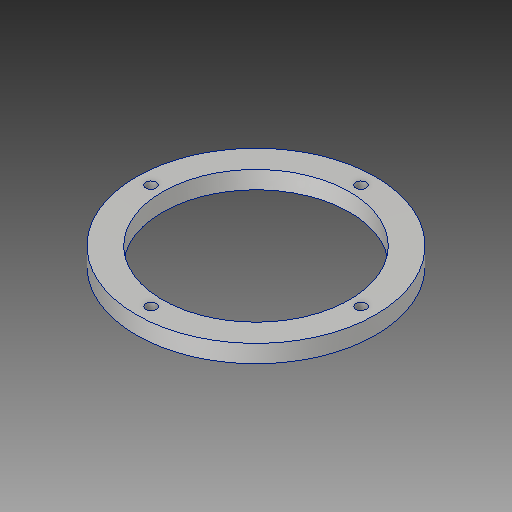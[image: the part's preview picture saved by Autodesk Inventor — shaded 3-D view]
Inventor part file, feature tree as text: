
AUTODESK INVENTOR PART (.ipt)
format: ipt  version: 2019 (Build 230136000, 136)  size: 104,960 bytes
history: native  units: mm
features: sketch x2, other x1, extrude x1, hole x1
ambient origin geometry x8: Origin, YZ Plane, XZ Plane, XY Plane, X Axis, Y Axis, Z Axis, Center Point
bodies: Body1 (feature_tree)
feature tree (5):
  other  "ソリッド1"
  extrude  "押し出し1"  Depth=90.0mm
  hole  "穴1"  [1 undecoded]
  sketch  "スケッチ1"
  sketch  "スケッチ2"
note: 1 required parameter value undecoded (feature->parameter linkage not recoverable at this tier; creation-order binding heuristic only, values carry confidence <= 0.55)
